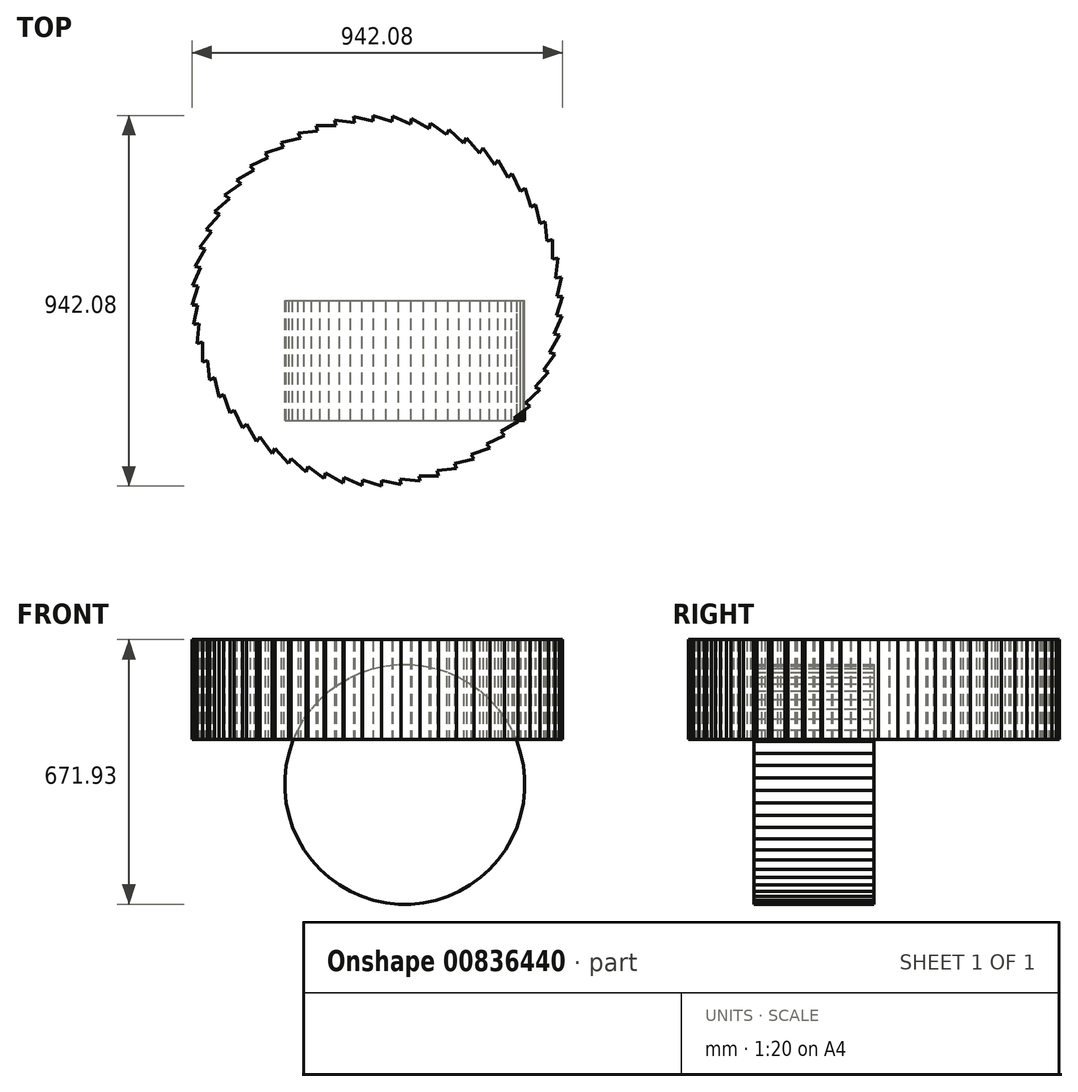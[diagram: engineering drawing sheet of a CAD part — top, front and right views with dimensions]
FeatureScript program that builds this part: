
annotation { "Feature Type Name" : "Feature", "Feature Type Description" : "" }
export const myFeature = defineFeature(function(context is Context, id is Id, definition is map)
    precondition{}
    {
        {
            var Q0;
            Q0=qCreatedBy(makeId("Top.planeOp"),FACE);
            var sketch = newSketch(context, id + "F0", { "sketchPlane" : qUnion([Q0])});
            skLineSegment(sketch, "E0", {"start": v(444.6, 105.4) * mm, "end": v(444.6, 156) * mm});
            skLineSegment(sketch, "E1", {"start": v(444.6, 156) * mm, "end": v(0, 0) * mm});
            skLineSegment(sketch, "E2", {"start": v(0, 0) * mm, "end": v(444.6, 105.4) * mm});
            skLineSegment(sketch, "E3.1.0", {"start": v(431.14, 151.29) * mm, "end": v(425.85, 201.63) * mm});
            skLineSegment(sketch, "E3.1.1", {"start": v(0, 0) * mm, "end": v(431.14, 151.29) * mm});
            skLineSegment(sketch, "E3.1.2", {"start": v(425.85, 201.63) * mm, "end": v(0, 0) * mm});
            skLineSegment(sketch, "E3.2.0", {"start": v(412.96, 195.53) * mm, "end": v(402.44, 245.04) * mm});
            skLineSegment(sketch, "E3.2.1", {"start": v(0, 0) * mm, "end": v(412.96, 195.53) * mm});
            skLineSegment(sketch, "E3.2.2", {"start": v(402.44, 245.04) * mm, "end": v(0, 0) * mm});
            skLineSegment(sketch, "E3.3.0", {"start": v(390.26, 237.62) * mm, "end": v(374.62, 285.76) * mm});
            skLineSegment(sketch, "E3.3.1", {"start": v(0, 0) * mm, "end": v(390.26, 237.62) * mm});
            skLineSegment(sketch, "E3.3.2", {"start": v(374.62, 285.76) * mm, "end": v(0, 0) * mm});
            skLineSegment(sketch, "E3.4.0", {"start": v(363.29, 277.11) * mm, "end": v(342.7, 323.35) * mm});
            skLineSegment(sketch, "E3.4.1", {"start": v(0, 0) * mm, "end": v(363.29, 277.11) * mm});
            skLineSegment(sketch, "E3.4.2", {"start": v(342.7, 323.35) * mm, "end": v(0, 0) * mm});
            skLineSegment(sketch, "E3.5.0", {"start": v(332.33, 313.57) * mm, "end": v(307.02, 357.4) * mm});
            skLineSegment(sketch, "E3.5.1", {"start": v(0, 0) * mm, "end": v(332.33, 313.57) * mm});
            skLineSegment(sketch, "E3.5.2", {"start": v(307.02, 357.4) * mm, "end": v(0, 0) * mm});
            skLineSegment(sketch, "E3.6.0", {"start": v(297.73, 346.59) * mm, "end": v(267.98, 387.54) * mm});
            skLineSegment(sketch, "E3.6.1", {"start": v(0, 0) * mm, "end": v(297.73, 346.59) * mm});
            skLineSegment(sketch, "E3.6.2", {"start": v(267.98, 387.54) * mm, "end": v(0, 0) * mm});
            skLineSegment(sketch, "E3.7.0", {"start": v(259.87, 375.81) * mm, "end": v(226, 413.43) * mm});
            skLineSegment(sketch, "E3.7.1", {"start": v(0, 0) * mm, "end": v(259.87, 375.81) * mm});
            skLineSegment(sketch, "E3.7.2", {"start": v(226, 413.43) * mm, "end": v(0, 0) * mm});
            skLineSegment(sketch, "E3.8.0", {"start": v(219.17, 400.92) * mm, "end": v(181.55, 434.79) * mm});
            skLineSegment(sketch, "E3.8.1", {"start": v(0, 0) * mm, "end": v(219.17, 400.92) * mm});
            skLineSegment(sketch, "E3.8.2", {"start": v(181.55, 434.79) * mm, "end": v(0, 0) * mm});
            skLineSegment(sketch, "E3.9.0", {"start": v(176.06, 421.63) * mm, "end": v(135.11, 451.38) * mm});
            skLineSegment(sketch, "E3.9.1", {"start": v(0, 0) * mm, "end": v(176.06, 421.63) * mm});
            skLineSegment(sketch, "E3.9.2", {"start": v(135.11, 451.38) * mm, "end": v(0, 0) * mm});
            skLineSegment(sketch, "E3.10.0", {"start": v(131.02, 437.72) * mm, "end": v(87.19, 463.03) * mm});
            skLineSegment(sketch, "E3.10.1", {"start": v(0, 0) * mm, "end": v(131.02, 437.72) * mm});
            skLineSegment(sketch, "E3.10.2", {"start": v(87.19, 463.03) * mm, "end": v(0, 0) * mm});
            skLineSegment(sketch, "E3.11.0", {"start": v(84.55, 449.02) * mm, "end": v(38.31, 469.6) * mm});
            skLineSegment(sketch, "E3.11.1", {"start": v(0, 0) * mm, "end": v(84.55, 449.02) * mm});
            skLineSegment(sketch, "E3.11.2", {"start": v(38.31, 469.6) * mm, "end": v(0, 0) * mm});
            skLineSegment(sketch, "E3.12.0", {"start": v(37.15, 455.4) * mm, "end": v(-10.99, 471.04) * mm});
            skLineSegment(sketch, "E3.12.1", {"start": v(0, 0) * mm, "end": v(37.15, 455.4) * mm});
            skLineSegment(sketch, "E3.12.2", {"start": v(-10.99, 471.04) * mm, "end": v(0, 0) * mm});
            skLineSegment(sketch, "E3.13.0", {"start": v(-10.65, 456.79) * mm, "end": v(-60.16, 467.31) * mm});
            skLineSegment(sketch, "E3.13.1", {"start": v(0, 0) * mm, "end": v(-10.65, 456.79) * mm});
            skLineSegment(sketch, "E3.13.2", {"start": v(-60.16, 467.31) * mm, "end": v(0, 0) * mm});
            skLineSegment(sketch, "E3.14.0", {"start": v(-58.34, 453.17) * mm, "end": v(-108.68, 458.46) * mm});
            skLineSegment(sketch, "E3.14.1", {"start": v(0, 0) * mm, "end": v(-58.34, 453.17) * mm});
            skLineSegment(sketch, "E3.14.2", {"start": v(-108.68, 458.46) * mm, "end": v(0, 0) * mm});
            skLineSegment(sketch, "E3.15.0", {"start": v(-105.4, 444.6) * mm, "end": v(-156, 444.6) * mm});
            skLineSegment(sketch, "E3.15.1", {"start": v(0, 0) * mm, "end": v(-105.4, 444.6) * mm});
            skLineSegment(sketch, "E3.15.2", {"start": v(-156, 444.6) * mm, "end": v(0, 0) * mm});
            skLineSegment(sketch, "E3.16.0", {"start": v(-151.29, 431.14) * mm, "end": v(-201.63, 425.85) * mm});
            skLineSegment(sketch, "E3.16.1", {"start": v(0, 0) * mm, "end": v(-151.29, 431.14) * mm});
            skLineSegment(sketch, "E3.16.2", {"start": v(-201.63, 425.85) * mm, "end": v(0, 0) * mm});
            skLineSegment(sketch, "E3.17.0", {"start": v(-195.53, 412.96) * mm, "end": v(-245.04, 402.44) * mm});
            skLineSegment(sketch, "E3.17.1", {"start": v(0, 0) * mm, "end": v(-195.53, 412.96) * mm});
            skLineSegment(sketch, "E3.17.2", {"start": v(-245.04, 402.44) * mm, "end": v(0, 0) * mm});
            skLineSegment(sketch, "E3.18.0", {"start": v(-237.62, 390.26) * mm, "end": v(-285.76, 374.62) * mm});
            skLineSegment(sketch, "E3.18.1", {"start": v(0, 0) * mm, "end": v(-237.62, 390.26) * mm});
            skLineSegment(sketch, "E3.18.2", {"start": v(-285.76, 374.62) * mm, "end": v(0, 0) * mm});
            skLineSegment(sketch, "E3.19.0", {"start": v(-277.11, 363.29) * mm, "end": v(-323.35, 342.7) * mm});
            skLineSegment(sketch, "E3.19.1", {"start": v(0, 0) * mm, "end": v(-277.11, 363.29) * mm});
            skLineSegment(sketch, "E3.19.2", {"start": v(-323.35, 342.7) * mm, "end": v(0, 0) * mm});
            skLineSegment(sketch, "E3.20.0", {"start": v(-313.57, 332.33) * mm, "end": v(-357.4, 307.02) * mm});
            skLineSegment(sketch, "E3.20.1", {"start": v(0, 0) * mm, "end": v(-313.57, 332.33) * mm});
            skLineSegment(sketch, "E3.20.2", {"start": v(-357.4, 307.02) * mm, "end": v(0, 0) * mm});
            skLineSegment(sketch, "E3.21.0", {"start": v(-346.59, 297.73) * mm, "end": v(-387.54, 267.98) * mm});
            skLineSegment(sketch, "E3.21.1", {"start": v(0, 0) * mm, "end": v(-346.59, 297.73) * mm});
            skLineSegment(sketch, "E3.21.2", {"start": v(-387.54, 267.98) * mm, "end": v(0, 0) * mm});
            skLineSegment(sketch, "E3.22.0", {"start": v(-375.81, 259.87) * mm, "end": v(-413.43, 226) * mm});
            skLineSegment(sketch, "E3.22.1", {"start": v(0, 0) * mm, "end": v(-375.81, 259.87) * mm});
            skLineSegment(sketch, "E3.22.2", {"start": v(-413.43, 226) * mm, "end": v(0, 0) * mm});
            skLineSegment(sketch, "E3.23.0", {"start": v(-400.92, 219.17) * mm, "end": v(-434.79, 181.55) * mm});
            skLineSegment(sketch, "E3.23.1", {"start": v(0, 0) * mm, "end": v(-400.92, 219.17) * mm});
            skLineSegment(sketch, "E3.23.2", {"start": v(-434.79, 181.55) * mm, "end": v(0, 0) * mm});
            skLineSegment(sketch, "E3.24.0", {"start": v(-421.63, 176.06) * mm, "end": v(-451.38, 135.11) * mm});
            skLineSegment(sketch, "E3.24.1", {"start": v(0, 0) * mm, "end": v(-421.63, 176.06) * mm});
            skLineSegment(sketch, "E3.24.2", {"start": v(-451.38, 135.11) * mm, "end": v(0, 0) * mm});
            skLineSegment(sketch, "E3.25.0", {"start": v(-437.72, 131.02) * mm, "end": v(-463.03, 87.19) * mm});
            skLineSegment(sketch, "E3.25.1", {"start": v(0, 0) * mm, "end": v(-437.72, 131.02) * mm});
            skLineSegment(sketch, "E3.25.2", {"start": v(-463.03, 87.19) * mm, "end": v(0, 0) * mm});
            skLineSegment(sketch, "E3.26.0", {"start": v(-449.02, 84.55) * mm, "end": v(-469.6, 38.31) * mm});
            skLineSegment(sketch, "E3.26.1", {"start": v(0, 0) * mm, "end": v(-449.02, 84.55) * mm});
            skLineSegment(sketch, "E3.26.2", {"start": v(-469.6, 38.31) * mm, "end": v(0, 0) * mm});
            skLineSegment(sketch, "E3.27.0", {"start": v(-455.4, 37.15) * mm, "end": v(-471.04, -10.99) * mm});
            skLineSegment(sketch, "E3.27.1", {"start": v(0, 0) * mm, "end": v(-455.4, 37.15) * mm});
            skLineSegment(sketch, "E3.27.2", {"start": v(-471.04, -10.99) * mm, "end": v(0, 0) * mm});
            skLineSegment(sketch, "E3.28.0", {"start": v(-456.79, -10.65) * mm, "end": v(-467.31, -60.16) * mm});
            skLineSegment(sketch, "E3.28.1", {"start": v(0, 0) * mm, "end": v(-456.79, -10.65) * mm});
            skLineSegment(sketch, "E3.28.2", {"start": v(-467.31, -60.16) * mm, "end": v(0, 0) * mm});
            skLineSegment(sketch, "E3.29.0", {"start": v(-453.17, -58.34) * mm, "end": v(-458.46, -108.68) * mm});
            skLineSegment(sketch, "E3.29.1", {"start": v(0, 0) * mm, "end": v(-453.17, -58.34) * mm});
            skLineSegment(sketch, "E3.29.2", {"start": v(-458.46, -108.68) * mm, "end": v(0, 0) * mm});
            skLineSegment(sketch, "E3.30.0", {"start": v(-444.6, -105.4) * mm, "end": v(-444.6, -156) * mm});
            skLineSegment(sketch, "E3.30.1", {"start": v(0, 0) * mm, "end": v(-444.6, -105.4) * mm});
            skLineSegment(sketch, "E3.30.2", {"start": v(-444.6, -156) * mm, "end": v(0, 0) * mm});
            skLineSegment(sketch, "E3.31.0", {"start": v(-431.14, -151.29) * mm, "end": v(-425.85, -201.63) * mm});
            skLineSegment(sketch, "E3.31.1", {"start": v(0, 0) * mm, "end": v(-431.14, -151.29) * mm});
            skLineSegment(sketch, "E3.31.2", {"start": v(-425.85, -201.63) * mm, "end": v(0, 0) * mm});
            skLineSegment(sketch, "E3.32.0", {"start": v(-412.96, -195.53) * mm, "end": v(-402.44, -245.04) * mm});
            skLineSegment(sketch, "E3.32.1", {"start": v(0, 0) * mm, "end": v(-412.96, -195.53) * mm});
            skLineSegment(sketch, "E3.32.2", {"start": v(-402.44, -245.04) * mm, "end": v(0, 0) * mm});
            skLineSegment(sketch, "E3.33.0", {"start": v(-390.26, -237.62) * mm, "end": v(-374.62, -285.76) * mm});
            skLineSegment(sketch, "E3.33.1", {"start": v(0, 0) * mm, "end": v(-390.26, -237.62) * mm});
            skLineSegment(sketch, "E3.33.2", {"start": v(-374.62, -285.76) * mm, "end": v(0, 0) * mm});
            skLineSegment(sketch, "E3.34.0", {"start": v(-363.29, -277.11) * mm, "end": v(-342.7, -323.35) * mm});
            skLineSegment(sketch, "E3.34.1", {"start": v(0, 0) * mm, "end": v(-363.29, -277.11) * mm});
            skLineSegment(sketch, "E3.34.2", {"start": v(-342.7, -323.35) * mm, "end": v(0, 0) * mm});
            skLineSegment(sketch, "E3.35.0", {"start": v(-332.33, -313.57) * mm, "end": v(-307.02, -357.4) * mm});
            skLineSegment(sketch, "E3.35.1", {"start": v(0, 0) * mm, "end": v(-332.33, -313.57) * mm});
            skLineSegment(sketch, "E3.35.2", {"start": v(-307.02, -357.4) * mm, "end": v(0, 0) * mm});
            skLineSegment(sketch, "E3.36.0", {"start": v(-297.73, -346.59) * mm, "end": v(-267.98, -387.54) * mm});
            skLineSegment(sketch, "E3.36.1", {"start": v(0, 0) * mm, "end": v(-297.73, -346.59) * mm});
            skLineSegment(sketch, "E3.36.2", {"start": v(-267.98, -387.54) * mm, "end": v(0, 0) * mm});
            skLineSegment(sketch, "E3.37.0", {"start": v(-259.87, -375.81) * mm, "end": v(-226, -413.43) * mm});
            skLineSegment(sketch, "E3.37.1", {"start": v(0, 0) * mm, "end": v(-259.87, -375.81) * mm});
            skLineSegment(sketch, "E3.37.2", {"start": v(-226, -413.43) * mm, "end": v(0, 0) * mm});
            skLineSegment(sketch, "E3.38.0", {"start": v(-219.17, -400.92) * mm, "end": v(-181.55, -434.79) * mm});
            skLineSegment(sketch, "E3.38.1", {"start": v(0, 0) * mm, "end": v(-219.17, -400.92) * mm});
            skLineSegment(sketch, "E3.38.2", {"start": v(-181.55, -434.79) * mm, "end": v(0, 0) * mm});
            skLineSegment(sketch, "E3.39.0", {"start": v(-176.06, -421.63) * mm, "end": v(-135.11, -451.38) * mm});
            skLineSegment(sketch, "E3.39.1", {"start": v(0, 0) * mm, "end": v(-176.06, -421.63) * mm});
            skLineSegment(sketch, "E3.39.2", {"start": v(-135.11, -451.38) * mm, "end": v(0, 0) * mm});
            skLineSegment(sketch, "E3.40.0", {"start": v(-131.02, -437.72) * mm, "end": v(-87.19, -463.03) * mm});
            skLineSegment(sketch, "E3.40.1", {"start": v(0, 0) * mm, "end": v(-131.02, -437.72) * mm});
            skLineSegment(sketch, "E3.40.2", {"start": v(-87.19, -463.03) * mm, "end": v(0, 0) * mm});
            skLineSegment(sketch, "E3.41.0", {"start": v(-84.55, -449.02) * mm, "end": v(-38.31, -469.6) * mm});
            skLineSegment(sketch, "E3.41.1", {"start": v(0, 0) * mm, "end": v(-84.55, -449.02) * mm});
            skLineSegment(sketch, "E3.41.2", {"start": v(-38.31, -469.6) * mm, "end": v(0, 0) * mm});
            skLineSegment(sketch, "E3.42.0", {"start": v(-37.15, -455.4) * mm, "end": v(10.99, -471.04) * mm});
            skLineSegment(sketch, "E3.42.1", {"start": v(0, 0) * mm, "end": v(-37.15, -455.4) * mm});
            skLineSegment(sketch, "E3.42.2", {"start": v(10.99, -471.04) * mm, "end": v(0, 0) * mm});
            skLineSegment(sketch, "E3.43.0", {"start": v(10.65, -456.79) * mm, "end": v(60.16, -467.31) * mm});
            skLineSegment(sketch, "E3.43.1", {"start": v(0, 0) * mm, "end": v(10.65, -456.79) * mm});
            skLineSegment(sketch, "E3.43.2", {"start": v(60.16, -467.31) * mm, "end": v(0, 0) * mm});
            skLineSegment(sketch, "E3.44.0", {"start": v(58.34, -453.17) * mm, "end": v(108.68, -458.46) * mm});
            skLineSegment(sketch, "E3.44.1", {"start": v(0, 0) * mm, "end": v(58.34, -453.17) * mm});
            skLineSegment(sketch, "E3.44.2", {"start": v(108.68, -458.46) * mm, "end": v(0, 0) * mm});
            skLineSegment(sketch, "E3.45.0", {"start": v(105.4, -444.6) * mm, "end": v(156, -444.6) * mm});
            skLineSegment(sketch, "E3.45.1", {"start": v(0, 0) * mm, "end": v(105.4, -444.6) * mm});
            skLineSegment(sketch, "E3.45.2", {"start": v(156, -444.6) * mm, "end": v(0, 0) * mm});
            skLineSegment(sketch, "E3.46.0", {"start": v(151.29, -431.14) * mm, "end": v(201.63, -425.85) * mm});
            skLineSegment(sketch, "E3.46.1", {"start": v(0, 0) * mm, "end": v(151.29, -431.14) * mm});
            skLineSegment(sketch, "E3.46.2", {"start": v(201.63, -425.85) * mm, "end": v(0, 0) * mm});
            skLineSegment(sketch, "E3.47.0", {"start": v(195.53, -412.96) * mm, "end": v(245.04, -402.44) * mm});
            skLineSegment(sketch, "E3.47.1", {"start": v(0, 0) * mm, "end": v(195.53, -412.96) * mm});
            skLineSegment(sketch, "E3.47.2", {"start": v(245.04, -402.44) * mm, "end": v(0, 0) * mm});
            skLineSegment(sketch, "E3.48.0", {"start": v(237.62, -390.26) * mm, "end": v(285.76, -374.62) * mm});
            skLineSegment(sketch, "E3.48.1", {"start": v(0, 0) * mm, "end": v(237.62, -390.26) * mm});
            skLineSegment(sketch, "E3.48.2", {"start": v(285.76, -374.62) * mm, "end": v(0, 0) * mm});
            skLineSegment(sketch, "E3.49.0", {"start": v(277.11, -363.29) * mm, "end": v(323.35, -342.7) * mm});
            skLineSegment(sketch, "E3.49.1", {"start": v(0, 0) * mm, "end": v(277.11, -363.29) * mm});
            skLineSegment(sketch, "E3.49.2", {"start": v(323.35, -342.7) * mm, "end": v(0, 0) * mm});
            skLineSegment(sketch, "E3.50.0", {"start": v(313.57, -332.33) * mm, "end": v(357.4, -307.02) * mm});
            skLineSegment(sketch, "E3.50.1", {"start": v(0, 0) * mm, "end": v(313.57, -332.33) * mm});
            skLineSegment(sketch, "E3.50.2", {"start": v(357.4, -307.02) * mm, "end": v(0, 0) * mm});
            skLineSegment(sketch, "E3.51.0", {"start": v(346.59, -297.73) * mm, "end": v(387.54, -267.98) * mm});
            skLineSegment(sketch, "E3.51.1", {"start": v(0, 0) * mm, "end": v(346.59, -297.73) * mm});
            skLineSegment(sketch, "E3.51.2", {"start": v(387.54, -267.98) * mm, "end": v(0, 0) * mm});
            skLineSegment(sketch, "E3.52.0", {"start": v(375.81, -259.87) * mm, "end": v(413.43, -226) * mm});
            skLineSegment(sketch, "E3.52.1", {"start": v(0, 0) * mm, "end": v(375.81, -259.87) * mm});
            skLineSegment(sketch, "E3.52.2", {"start": v(413.43, -226) * mm, "end": v(0, 0) * mm});
            skLineSegment(sketch, "E3.53.0", {"start": v(400.92, -219.17) * mm, "end": v(434.79, -181.55) * mm});
            skLineSegment(sketch, "E3.53.1", {"start": v(0, 0) * mm, "end": v(400.92, -219.17) * mm});
            skLineSegment(sketch, "E3.53.2", {"start": v(434.79, -181.55) * mm, "end": v(0, 0) * mm});
            skLineSegment(sketch, "E3.54.0", {"start": v(421.63, -176.06) * mm, "end": v(451.38, -135.11) * mm});
            skLineSegment(sketch, "E3.54.1", {"start": v(0, 0) * mm, "end": v(421.63, -176.06) * mm});
            skLineSegment(sketch, "E3.54.2", {"start": v(451.38, -135.11) * mm, "end": v(0, 0) * mm});
            skLineSegment(sketch, "E3.55.0", {"start": v(437.72, -131.02) * mm, "end": v(463.03, -87.19) * mm});
            skLineSegment(sketch, "E3.55.1", {"start": v(0, 0) * mm, "end": v(437.72, -131.02) * mm});
            skLineSegment(sketch, "E3.55.2", {"start": v(463.03, -87.19) * mm, "end": v(0, 0) * mm});
            skLineSegment(sketch, "E3.56.0", {"start": v(449.02, -84.55) * mm, "end": v(469.6, -38.31) * mm});
            skLineSegment(sketch, "E3.56.1", {"start": v(0, 0) * mm, "end": v(449.02, -84.55) * mm});
            skLineSegment(sketch, "E3.56.2", {"start": v(469.6, -38.31) * mm, "end": v(0, 0) * mm});
            skLineSegment(sketch, "E3.57.0", {"start": v(455.4, -37.15) * mm, "end": v(471.04, 10.99) * mm});
            skLineSegment(sketch, "E3.57.1", {"start": v(0, 0) * mm, "end": v(455.4, -37.15) * mm});
            skLineSegment(sketch, "E3.57.2", {"start": v(471.04, 10.99) * mm, "end": v(0, 0) * mm});
            skLineSegment(sketch, "E3.58.0", {"start": v(456.79, 10.65) * mm, "end": v(467.31, 60.16) * mm});
            skLineSegment(sketch, "E3.58.1", {"start": v(0, 0) * mm, "end": v(456.79, 10.65) * mm});
            skLineSegment(sketch, "E3.58.2", {"start": v(467.31, 60.16) * mm, "end": v(0, 0) * mm});
            skLineSegment(sketch, "E3.59.0", {"start": v(453.17, 58.34) * mm, "end": v(458.46, 108.68) * mm});
            skLineSegment(sketch, "E3.59.1", {"start": v(0, 0) * mm, "end": v(453.17, 58.34) * mm});
            skLineSegment(sketch, "E3.59.2", {"start": v(458.46, 108.68) * mm, "end": v(0, 0) * mm});
            skPoint(sketch, "E3.center", {"position": v(0, 0) * mm});
            skSolve(sketch);
        }
        {
            var Q0;
            Q0 = qSketchRegion(id + "F0", true);
            extrude(context, id + "F1", {"entities" : qUnion([Q0]), "depth" : 254 * mm, "offsetDistance" : 25.4 * mm});
        }
        {
            var Q0;
            Q0=qCreatedBy(makeId("Front.planeOp"),FACE);
            var sketch = newSketch(context, id + "F2", { "sketchPlane" : qUnion([Q0])});
            skLineSegment(sketch, "E4", {"start": v(374.16, -97.6) * mm, "end": v(374.16, -129.5) * mm});
            skLineSegment(sketch, "E5", {"start": v(374.16, -129.5) * mm, "end": v(69.78, -113.55) * mm});
            skLineSegment(sketch, "E6", {"start": v(69.78, -113.55) * mm, "end": v(374.16, -97.6) * mm});
            skLineSegment(sketch, "E7.1.0", {"start": v(370.82, -65.87) * mm, "end": v(374.16, -97.6) * mm});
            skLineSegment(sketch, "E7.1.1", {"start": v(69.78, -113.55) * mm, "end": v(370.82, -65.87) * mm});
            skLineSegment(sketch, "E7.1.2", {"start": v(374.16, -97.6) * mm, "end": v(69.78, -113.55) * mm});
            skLineSegment(sketch, "E7.2.0", {"start": v(364.2, -34.66) * mm, "end": v(370.82, -65.87) * mm});
            skLineSegment(sketch, "E7.2.1", {"start": v(69.78, -113.55) * mm, "end": v(364.2, -34.66) * mm});
            skLineSegment(sketch, "E7.2.2", {"start": v(370.82, -65.87) * mm, "end": v(69.78, -113.55) * mm});
            skLineSegment(sketch, "E7.3.0", {"start": v(354.33, -4.32) * mm, "end": v(364.2, -34.66) * mm});
            skLineSegment(sketch, "E7.3.1", {"start": v(69.78, -113.55) * mm, "end": v(354.33, -4.32) * mm});
            skLineSegment(sketch, "E7.3.2", {"start": v(364.2, -34.66) * mm, "end": v(69.78, -113.55) * mm});
            skLineSegment(sketch, "E7.4.0", {"start": v(341.36, 24.83) * mm, "end": v(354.33, -4.32) * mm});
            skLineSegment(sketch, "E7.4.1", {"start": v(69.78, -113.55) * mm, "end": v(341.36, 24.83) * mm});
            skLineSegment(sketch, "E7.4.2", {"start": v(354.33, -4.32) * mm, "end": v(69.78, -113.55) * mm});
            skLineSegment(sketch, "E7.5.0", {"start": v(325.4, 52.46) * mm, "end": v(341.36, 24.83) * mm});
            skLineSegment(sketch, "E7.5.1", {"start": v(69.78, -113.55) * mm, "end": v(325.4, 52.46) * mm});
            skLineSegment(sketch, "E7.5.2", {"start": v(341.36, 24.83) * mm, "end": v(69.78, -113.55) * mm});
            skLineSegment(sketch, "E7.6.0", {"start": v(306.65, 78.27) * mm, "end": v(325.4, 52.46) * mm});
            skLineSegment(sketch, "E7.6.1", {"start": v(69.78, -113.55) * mm, "end": v(306.65, 78.27) * mm});
            skLineSegment(sketch, "E7.6.2", {"start": v(325.4, 52.46) * mm, "end": v(69.78, -113.55) * mm});
            skLineSegment(sketch, "E7.7.0", {"start": v(285.3, 101.98) * mm, "end": v(306.65, 78.27) * mm});
            skLineSegment(sketch, "E7.7.1", {"start": v(69.78, -113.55) * mm, "end": v(285.3, 101.98) * mm});
            skLineSegment(sketch, "E7.7.2", {"start": v(306.65, 78.27) * mm, "end": v(69.78, -113.55) * mm});
            skLineSegment(sketch, "E7.8.0", {"start": v(261.6, 123.33) * mm, "end": v(285.3, 101.98) * mm});
            skLineSegment(sketch, "E7.8.1", {"start": v(69.78, -113.55) * mm, "end": v(261.6, 123.33) * mm});
            skLineSegment(sketch, "E7.8.2", {"start": v(285.3, 101.98) * mm, "end": v(69.78, -113.55) * mm});
            skLineSegment(sketch, "E7.9.0", {"start": v(235.78, 142.08) * mm, "end": v(261.6, 123.33) * mm});
            skLineSegment(sketch, "E7.9.1", {"start": v(69.78, -113.55) * mm, "end": v(235.78, 142.08) * mm});
            skLineSegment(sketch, "E7.9.2", {"start": v(261.6, 123.33) * mm, "end": v(69.78, -113.55) * mm});
            skLineSegment(sketch, "E7.10.0", {"start": v(208.15, 158.03) * mm, "end": v(235.78, 142.08) * mm});
            skLineSegment(sketch, "E7.10.1", {"start": v(69.78, -113.55) * mm, "end": v(208.15, 158.03) * mm});
            skLineSegment(sketch, "E7.10.2", {"start": v(235.78, 142.08) * mm, "end": v(69.78, -113.55) * mm});
            skLineSegment(sketch, "E7.11.0", {"start": v(179, 171) * mm, "end": v(208.15, 158.03) * mm});
            skLineSegment(sketch, "E7.11.1", {"start": v(69.78, -113.55) * mm, "end": v(179, 171) * mm});
            skLineSegment(sketch, "E7.11.2", {"start": v(208.15, 158.03) * mm, "end": v(69.78, -113.55) * mm});
            skLineSegment(sketch, "E7.12.0", {"start": v(148.66, 180.87) * mm, "end": v(179, 171) * mm});
            skLineSegment(sketch, "E7.12.1", {"start": v(69.78, -113.55) * mm, "end": v(148.66, 180.87) * mm});
            skLineSegment(sketch, "E7.12.2", {"start": v(179, 171) * mm, "end": v(69.78, -113.55) * mm});
            skLineSegment(sketch, "E7.13.0", {"start": v(117.46, 187.5) * mm, "end": v(148.66, 180.87) * mm});
            skLineSegment(sketch, "E7.13.1", {"start": v(69.78, -113.55) * mm, "end": v(117.46, 187.5) * mm});
            skLineSegment(sketch, "E7.13.2", {"start": v(148.66, 180.87) * mm, "end": v(69.78, -113.55) * mm});
            skLineSegment(sketch, "E7.14.0", {"start": v(85.73, 190.83) * mm, "end": v(117.46, 187.5) * mm});
            skLineSegment(sketch, "E7.14.1", {"start": v(69.78, -113.55) * mm, "end": v(85.73, 190.83) * mm});
            skLineSegment(sketch, "E7.14.2", {"start": v(117.46, 187.5) * mm, "end": v(69.78, -113.55) * mm});
            skLineSegment(sketch, "E7.15.0", {"start": v(53.82, 190.83) * mm, "end": v(85.73, 190.83) * mm});
            skLineSegment(sketch, "E7.15.1", {"start": v(69.78, -113.55) * mm, "end": v(53.82, 190.83) * mm});
            skLineSegment(sketch, "E7.15.2", {"start": v(85.73, 190.83) * mm, "end": v(69.78, -113.55) * mm});
            skLineSegment(sketch, "E7.16.0", {"start": v(22.1, 187.5) * mm, "end": v(53.82, 190.83) * mm});
            skLineSegment(sketch, "E7.16.1", {"start": v(69.78, -113.55) * mm, "end": v(22.1, 187.5) * mm});
            skLineSegment(sketch, "E7.16.2", {"start": v(53.82, 190.83) * mm, "end": v(69.78, -113.55) * mm});
            skLineSegment(sketch, "E7.17.0", {"start": v(-9.11, 180.87) * mm, "end": v(22.1, 187.5) * mm});
            skLineSegment(sketch, "E7.17.1", {"start": v(69.78, -113.55) * mm, "end": v(-9.11, 180.87) * mm});
            skLineSegment(sketch, "E7.17.2", {"start": v(22.1, 187.5) * mm, "end": v(69.78, -113.55) * mm});
            skLineSegment(sketch, "E7.18.0", {"start": v(-39.45, 171) * mm, "end": v(-9.11, 180.87) * mm});
            skLineSegment(sketch, "E7.18.1", {"start": v(69.78, -113.55) * mm, "end": v(-39.45, 171) * mm});
            skLineSegment(sketch, "E7.18.2", {"start": v(-9.11, 180.87) * mm, "end": v(69.78, -113.55) * mm});
            skLineSegment(sketch, "E7.19.0", {"start": v(-68.6, 158.03) * mm, "end": v(-39.45, 171) * mm});
            skLineSegment(sketch, "E7.19.1", {"start": v(69.78, -113.55) * mm, "end": v(-68.6, 158.03) * mm});
            skLineSegment(sketch, "E7.19.2", {"start": v(-39.45, 171) * mm, "end": v(69.78, -113.55) * mm});
            skLineSegment(sketch, "E7.20.0", {"start": v(-96.23, 142.08) * mm, "end": v(-68.6, 158.03) * mm});
            skLineSegment(sketch, "E7.20.1", {"start": v(69.78, -113.55) * mm, "end": v(-96.23, 142.08) * mm});
            skLineSegment(sketch, "E7.20.2", {"start": v(-68.6, 158.03) * mm, "end": v(69.78, -113.55) * mm});
            skLineSegment(sketch, "E7.21.0", {"start": v(-122.04, 123.33) * mm, "end": v(-96.23, 142.08) * mm});
            skLineSegment(sketch, "E7.21.1", {"start": v(69.78, -113.55) * mm, "end": v(-122.04, 123.33) * mm});
            skLineSegment(sketch, "E7.21.2", {"start": v(-96.23, 142.08) * mm, "end": v(69.78, -113.55) * mm});
            skLineSegment(sketch, "E7.22.0", {"start": v(-145.75, 101.98) * mm, "end": v(-122.04, 123.33) * mm});
            skLineSegment(sketch, "E7.22.1", {"start": v(69.78, -113.55) * mm, "end": v(-145.75, 101.98) * mm});
            skLineSegment(sketch, "E7.22.2", {"start": v(-122.04, 123.33) * mm, "end": v(69.78, -113.55) * mm});
            skLineSegment(sketch, "E7.23.0", {"start": v(-167.1, 78.27) * mm, "end": v(-145.75, 101.98) * mm});
            skLineSegment(sketch, "E7.23.1", {"start": v(69.78, -113.55) * mm, "end": v(-167.1, 78.27) * mm});
            skLineSegment(sketch, "E7.23.2", {"start": v(-145.75, 101.98) * mm, "end": v(69.78, -113.55) * mm});
            skLineSegment(sketch, "E7.24.0", {"start": v(-185.85, 52.46) * mm, "end": v(-167.1, 78.27) * mm});
            skLineSegment(sketch, "E7.24.1", {"start": v(69.78, -113.55) * mm, "end": v(-185.85, 52.46) * mm});
            skLineSegment(sketch, "E7.24.2", {"start": v(-167.1, 78.27) * mm, "end": v(69.78, -113.55) * mm});
            skLineSegment(sketch, "E7.25.0", {"start": v(-201.8, 24.83) * mm, "end": v(-185.85, 52.46) * mm});
            skLineSegment(sketch, "E7.25.1", {"start": v(69.78, -113.55) * mm, "end": v(-201.8, 24.83) * mm});
            skLineSegment(sketch, "E7.25.2", {"start": v(-185.85, 52.46) * mm, "end": v(69.78, -113.55) * mm});
            skLineSegment(sketch, "E7.26.0", {"start": v(-214.78, -4.32) * mm, "end": v(-201.8, 24.83) * mm});
            skLineSegment(sketch, "E7.26.1", {"start": v(69.78, -113.55) * mm, "end": v(-214.78, -4.32) * mm});
            skLineSegment(sketch, "E7.26.2", {"start": v(-201.8, 24.83) * mm, "end": v(69.78, -113.55) * mm});
            skLineSegment(sketch, "E7.27.0", {"start": v(-224.64, -34.66) * mm, "end": v(-214.78, -4.32) * mm});
            skLineSegment(sketch, "E7.27.1", {"start": v(69.78, -113.55) * mm, "end": v(-224.64, -34.66) * mm});
            skLineSegment(sketch, "E7.27.2", {"start": v(-214.78, -4.32) * mm, "end": v(69.78, -113.55) * mm});
            skLineSegment(sketch, "E7.28.0", {"start": v(-231.27, -65.87) * mm, "end": v(-224.64, -34.66) * mm});
            skLineSegment(sketch, "E7.28.1", {"start": v(69.78, -113.55) * mm, "end": v(-231.27, -65.87) * mm});
            skLineSegment(sketch, "E7.28.2", {"start": v(-224.64, -34.66) * mm, "end": v(69.78, -113.55) * mm});
            skLineSegment(sketch, "E7.29.0", {"start": v(-234.6, -97.6) * mm, "end": v(-231.27, -65.87) * mm});
            skLineSegment(sketch, "E7.29.1", {"start": v(69.78, -113.55) * mm, "end": v(-234.6, -97.6) * mm});
            skLineSegment(sketch, "E7.29.2", {"start": v(-231.27, -65.87) * mm, "end": v(69.78, -113.55) * mm});
            skLineSegment(sketch, "E7.30.0", {"start": v(-234.6, -129.5) * mm, "end": v(-234.6, -97.6) * mm});
            skLineSegment(sketch, "E7.30.1", {"start": v(69.78, -113.55) * mm, "end": v(-234.6, -129.5) * mm});
            skLineSegment(sketch, "E7.30.2", {"start": v(-234.6, -97.6) * mm, "end": v(69.78, -113.55) * mm});
            skLineSegment(sketch, "E7.31.0", {"start": v(-231.27, -161.23) * mm, "end": v(-234.6, -129.5) * mm});
            skLineSegment(sketch, "E7.31.1", {"start": v(69.78, -113.55) * mm, "end": v(-231.27, -161.23) * mm});
            skLineSegment(sketch, "E7.31.2", {"start": v(-234.6, -129.5) * mm, "end": v(69.78, -113.55) * mm});
            skLineSegment(sketch, "E7.32.0", {"start": v(-224.64, -192.44) * mm, "end": v(-231.27, -161.23) * mm});
            skLineSegment(sketch, "E7.32.1", {"start": v(69.78, -113.55) * mm, "end": v(-224.64, -192.44) * mm});
            skLineSegment(sketch, "E7.32.2", {"start": v(-231.27, -161.23) * mm, "end": v(69.78, -113.55) * mm});
            skLineSegment(sketch, "E7.33.0", {"start": v(-214.78, -222.78) * mm, "end": v(-224.64, -192.44) * mm});
            skLineSegment(sketch, "E7.33.1", {"start": v(69.78, -113.55) * mm, "end": v(-214.78, -222.78) * mm});
            skLineSegment(sketch, "E7.33.2", {"start": v(-224.64, -192.44) * mm, "end": v(69.78, -113.55) * mm});
            skLineSegment(sketch, "E7.34.0", {"start": v(-201.8, -251.92) * mm, "end": v(-214.78, -222.78) * mm});
            skLineSegment(sketch, "E7.34.1", {"start": v(69.78, -113.55) * mm, "end": v(-201.8, -251.92) * mm});
            skLineSegment(sketch, "E7.34.2", {"start": v(-214.78, -222.78) * mm, "end": v(69.78, -113.55) * mm});
            skLineSegment(sketch, "E7.35.0", {"start": v(-185.85, -279.55) * mm, "end": v(-201.8, -251.92) * mm});
            skLineSegment(sketch, "E7.35.1", {"start": v(69.78, -113.55) * mm, "end": v(-185.85, -279.55) * mm});
            skLineSegment(sketch, "E7.35.2", {"start": v(-201.8, -251.92) * mm, "end": v(69.78, -113.55) * mm});
            skLineSegment(sketch, "E7.36.0", {"start": v(-167.1, -305.36) * mm, "end": v(-185.85, -279.55) * mm});
            skLineSegment(sketch, "E7.36.1", {"start": v(69.78, -113.55) * mm, "end": v(-167.1, -305.36) * mm});
            skLineSegment(sketch, "E7.36.2", {"start": v(-185.85, -279.55) * mm, "end": v(69.78, -113.55) * mm});
            skLineSegment(sketch, "E7.37.0", {"start": v(-145.75, -329.07) * mm, "end": v(-167.1, -305.36) * mm});
            skLineSegment(sketch, "E7.37.1", {"start": v(69.78, -113.55) * mm, "end": v(-145.75, -329.07) * mm});
            skLineSegment(sketch, "E7.37.2", {"start": v(-167.1, -305.36) * mm, "end": v(69.78, -113.55) * mm});
            skLineSegment(sketch, "E7.38.0", {"start": v(-122.04, -350.42) * mm, "end": v(-145.75, -329.07) * mm});
            skLineSegment(sketch, "E7.38.1", {"start": v(69.78, -113.55) * mm, "end": v(-122.04, -350.42) * mm});
            skLineSegment(sketch, "E7.38.2", {"start": v(-145.75, -329.07) * mm, "end": v(69.78, -113.55) * mm});
            skLineSegment(sketch, "E7.39.0", {"start": v(-96.23, -369.17) * mm, "end": v(-122.04, -350.42) * mm});
            skLineSegment(sketch, "E7.39.1", {"start": v(69.78, -113.55) * mm, "end": v(-96.23, -369.17) * mm});
            skLineSegment(sketch, "E7.39.2", {"start": v(-122.04, -350.42) * mm, "end": v(69.78, -113.55) * mm});
            skLineSegment(sketch, "E7.40.0", {"start": v(-68.6, -385.13) * mm, "end": v(-96.23, -369.17) * mm});
            skLineSegment(sketch, "E7.40.1", {"start": v(69.78, -113.55) * mm, "end": v(-68.6, -385.13) * mm});
            skLineSegment(sketch, "E7.40.2", {"start": v(-96.23, -369.17) * mm, "end": v(69.78, -113.55) * mm});
            skLineSegment(sketch, "E7.41.0", {"start": v(-39.45, -398.1) * mm, "end": v(-68.6, -385.13) * mm});
            skLineSegment(sketch, "E7.41.1", {"start": v(69.78, -113.55) * mm, "end": v(-39.45, -398.1) * mm});
            skLineSegment(sketch, "E7.41.2", {"start": v(-68.6, -385.13) * mm, "end": v(69.78, -113.55) * mm});
            skLineSegment(sketch, "E7.42.0", {"start": v(-9.11, -407.96) * mm, "end": v(-39.45, -398.1) * mm});
            skLineSegment(sketch, "E7.42.1", {"start": v(69.78, -113.55) * mm, "end": v(-9.11, -407.96) * mm});
            skLineSegment(sketch, "E7.42.2", {"start": v(-39.45, -398.1) * mm, "end": v(69.78, -113.55) * mm});
            skLineSegment(sketch, "E7.43.0", {"start": v(22.1, -414.6) * mm, "end": v(-9.11, -407.96) * mm});
            skLineSegment(sketch, "E7.43.1", {"start": v(69.78, -113.55) * mm, "end": v(22.1, -414.6) * mm});
            skLineSegment(sketch, "E7.43.2", {"start": v(-9.11, -407.96) * mm, "end": v(69.78, -113.55) * mm});
            skLineSegment(sketch, "E7.44.0", {"start": v(53.82, -417.93) * mm, "end": v(22.1, -414.6) * mm});
            skLineSegment(sketch, "E7.44.1", {"start": v(69.78, -113.55) * mm, "end": v(53.82, -417.93) * mm});
            skLineSegment(sketch, "E7.44.2", {"start": v(22.1, -414.6) * mm, "end": v(69.78, -113.55) * mm});
            skLineSegment(sketch, "E7.45.0", {"start": v(85.73, -417.93) * mm, "end": v(53.82, -417.93) * mm});
            skLineSegment(sketch, "E7.45.1", {"start": v(69.78, -113.55) * mm, "end": v(85.73, -417.93) * mm});
            skLineSegment(sketch, "E7.45.2", {"start": v(53.82, -417.93) * mm, "end": v(69.78, -113.55) * mm});
            skLineSegment(sketch, "E7.46.0", {"start": v(117.46, -414.6) * mm, "end": v(85.73, -417.93) * mm});
            skLineSegment(sketch, "E7.46.1", {"start": v(69.78, -113.55) * mm, "end": v(117.46, -414.6) * mm});
            skLineSegment(sketch, "E7.46.2", {"start": v(85.73, -417.93) * mm, "end": v(69.78, -113.55) * mm});
            skLineSegment(sketch, "E7.47.0", {"start": v(148.66, -407.96) * mm, "end": v(117.46, -414.6) * mm});
            skLineSegment(sketch, "E7.47.1", {"start": v(69.78, -113.55) * mm, "end": v(148.66, -407.96) * mm});
            skLineSegment(sketch, "E7.47.2", {"start": v(117.46, -414.6) * mm, "end": v(69.78, -113.55) * mm});
            skLineSegment(sketch, "E7.48.0", {"start": v(179, -398.1) * mm, "end": v(148.66, -407.96) * mm});
            skLineSegment(sketch, "E7.48.1", {"start": v(69.78, -113.55) * mm, "end": v(179, -398.1) * mm});
            skLineSegment(sketch, "E7.48.2", {"start": v(148.66, -407.96) * mm, "end": v(69.78, -113.55) * mm});
            skLineSegment(sketch, "E7.49.0", {"start": v(208.15, -385.13) * mm, "end": v(179, -398.1) * mm});
            skLineSegment(sketch, "E7.49.1", {"start": v(69.78, -113.55) * mm, "end": v(208.15, -385.13) * mm});
            skLineSegment(sketch, "E7.49.2", {"start": v(179, -398.1) * mm, "end": v(69.78, -113.55) * mm});
            skLineSegment(sketch, "E7.50.0", {"start": v(235.78, -369.17) * mm, "end": v(208.15, -385.13) * mm});
            skLineSegment(sketch, "E7.50.1", {"start": v(69.78, -113.55) * mm, "end": v(235.78, -369.17) * mm});
            skLineSegment(sketch, "E7.50.2", {"start": v(208.15, -385.13) * mm, "end": v(69.78, -113.55) * mm});
            skLineSegment(sketch, "E7.51.0", {"start": v(261.6, -350.42) * mm, "end": v(235.78, -369.17) * mm});
            skLineSegment(sketch, "E7.51.1", {"start": v(69.78, -113.55) * mm, "end": v(261.6, -350.42) * mm});
            skLineSegment(sketch, "E7.51.2", {"start": v(235.78, -369.17) * mm, "end": v(69.78, -113.55) * mm});
            skLineSegment(sketch, "E7.52.0", {"start": v(285.3, -329.07) * mm, "end": v(261.6, -350.42) * mm});
            skLineSegment(sketch, "E7.52.1", {"start": v(69.78, -113.55) * mm, "end": v(285.3, -329.07) * mm});
            skLineSegment(sketch, "E7.52.2", {"start": v(261.6, -350.42) * mm, "end": v(69.78, -113.55) * mm});
            skLineSegment(sketch, "E7.53.0", {"start": v(306.65, -305.36) * mm, "end": v(285.3, -329.07) * mm});
            skLineSegment(sketch, "E7.53.1", {"start": v(69.78, -113.55) * mm, "end": v(306.65, -305.36) * mm});
            skLineSegment(sketch, "E7.53.2", {"start": v(285.3, -329.07) * mm, "end": v(69.78, -113.55) * mm});
            skLineSegment(sketch, "E7.54.0", {"start": v(325.4, -279.55) * mm, "end": v(306.65, -305.36) * mm});
            skLineSegment(sketch, "E7.54.1", {"start": v(69.78, -113.55) * mm, "end": v(325.4, -279.55) * mm});
            skLineSegment(sketch, "E7.54.2", {"start": v(306.65, -305.36) * mm, "end": v(69.78, -113.55) * mm});
            skLineSegment(sketch, "E7.55.0", {"start": v(341.36, -251.92) * mm, "end": v(325.4, -279.55) * mm});
            skLineSegment(sketch, "E7.55.1", {"start": v(69.78, -113.55) * mm, "end": v(341.36, -251.92) * mm});
            skLineSegment(sketch, "E7.55.2", {"start": v(325.4, -279.55) * mm, "end": v(69.78, -113.55) * mm});
            skLineSegment(sketch, "E7.56.0", {"start": v(354.33, -222.78) * mm, "end": v(341.36, -251.92) * mm});
            skLineSegment(sketch, "E7.56.1", {"start": v(69.78, -113.55) * mm, "end": v(354.33, -222.78) * mm});
            skLineSegment(sketch, "E7.56.2", {"start": v(341.36, -251.92) * mm, "end": v(69.78, -113.55) * mm});
            skLineSegment(sketch, "E7.57.0", {"start": v(364.2, -192.44) * mm, "end": v(354.33, -222.78) * mm});
            skLineSegment(sketch, "E7.57.1", {"start": v(69.78, -113.55) * mm, "end": v(364.2, -192.44) * mm});
            skLineSegment(sketch, "E7.57.2", {"start": v(354.33, -222.78) * mm, "end": v(69.78, -113.55) * mm});
            skLineSegment(sketch, "E7.58.0", {"start": v(370.82, -161.23) * mm, "end": v(364.2, -192.44) * mm});
            skLineSegment(sketch, "E7.58.1", {"start": v(69.78, -113.55) * mm, "end": v(370.82, -161.23) * mm});
            skLineSegment(sketch, "E7.58.2", {"start": v(364.2, -192.44) * mm, "end": v(69.78, -113.55) * mm});
            skLineSegment(sketch, "E7.59.0", {"start": v(374.16, -129.5) * mm, "end": v(370.82, -161.23) * mm});
            skLineSegment(sketch, "E7.59.1", {"start": v(69.78, -113.55) * mm, "end": v(374.16, -129.5) * mm});
            skLineSegment(sketch, "E7.59.2", {"start": v(370.82, -161.23) * mm, "end": v(69.78, -113.55) * mm});
            skPoint(sketch, "E7.center", {"position": v(69.78, -113.55) * mm});
            skLineSegment(sketch, "E8", {"start": v(69.78, -113.55) * mm, "end": v(0, 0) * mm, "construction": true});
            skSolve(sketch);
        }
        {
            var Q0;
            Q0 = qSketchRegion(id + "F2", true);
            extrude(context, id + "F3", {"entities" : qUnion([Q0]), "depth" : 304.8 * mm, "offsetDistance" : 25.4 * mm});
        }
    });
